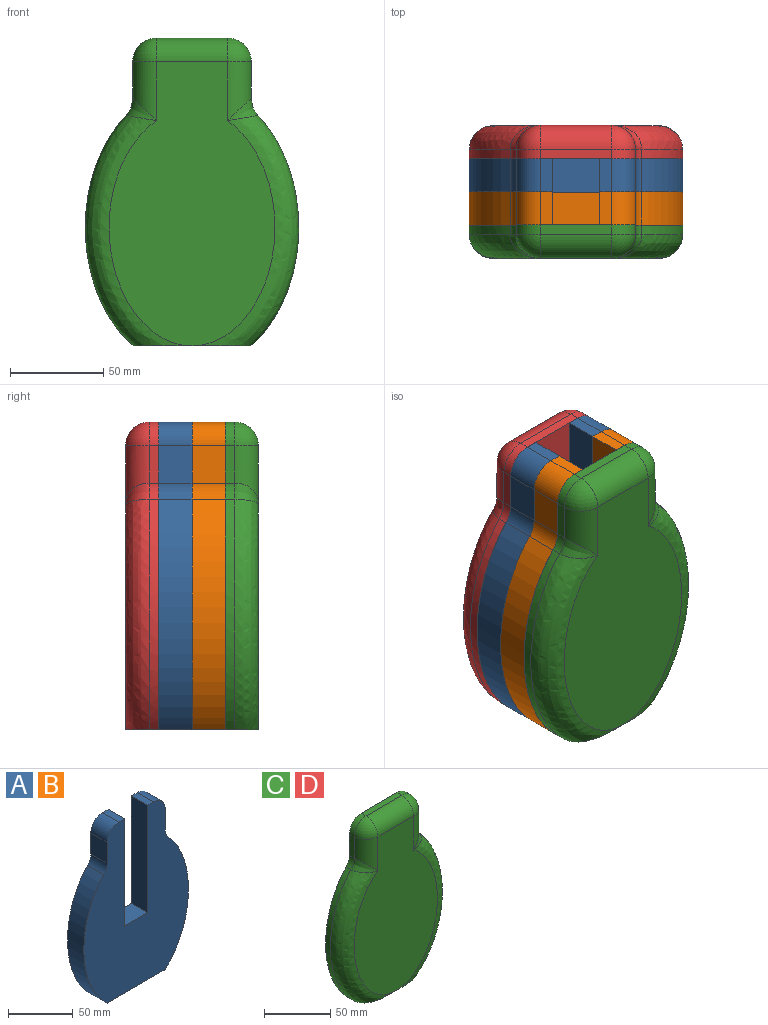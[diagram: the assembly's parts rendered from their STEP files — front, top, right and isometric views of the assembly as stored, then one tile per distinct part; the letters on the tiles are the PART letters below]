
ASSEMBLY  parts=4 mates=6
PART A: 16 faces, bbox 114.3x17.8x165 mm
  f0: plane 17.78x6.35mm, normal (0,0,1), area 112.9mm2, adj f7,f8,f12,f13
  f1: extruded ~123.46x25.55mm, area 2414.5mm2, adj f6,f7,f8,f10
  f2: plane 20.03x17.78mm, normal (1,0,0), area 356mm2, adj f7,f8,f10,f11
  f3: plane 17.78x6.35mm, normal (0,0,1), area 112.9mm2, adj f7,f8,f11,f15
  f4: plane 20.03x17.78mm, normal (-1,0,0), area 356mm2, adj f7,f8,f9,f12
  f5: extruded ~123.46x25.55mm, area 2414.5mm2, adj f6,f7,f8,f9
  f6: plane 63.18x17.78mm, normal (0,0,-1), area 1123.4mm2, adj f1,f5,f7,f8
  f7: plane 164.96x114.3mm, normal (0,-1,0), area 12359.6mm2, adj f0,f1,f2,f3,f4,f5,f6,f9
  f8: plane 164.96x114.3mm, normal (0,1,0), area 12359.6mm2, adj f0,f1,f2,f3,f4,f5,f6,f9
  f9: cylinder r=12.7mm len=17.78mm, axis (0,1,0), area 172.3mm2, adj f4,f5,f7,f8
  f10: cylinder r=12.7mm len=17.78mm, axis (0,1,0), area 172.3mm2, adj f1,f2,f7,f8
  f11: cylinder r=12.7mm len=17.78mm, axis (0,1,0), area 354.7mm2, adj f2,f3,f7,f8
  f12: cylinder r=12.7mm len=17.78mm, axis (0,-1,0), area 354.7mm2, adj f0,f4,f7,f8
  f13: plane 101.6x17.78mm, normal (1,0,0), area 1806.4mm2, adj f0,f7,f8,f14
  f14: plane 25.4x17.78mm, normal (0,0,1), area 451.6mm2, adj f7,f8,f13,f15
  f15: plane 101.6x17.78mm, normal (-1,0,0), area 1806.4mm2, adj f3,f7,f8,f14
PART B: same geometry as A
PART C: 21 faces, bbox 128.2x31.7x191.6 mm
  f0: extruded ~123.46x25.55mm, area 689.8mm2, adj f5,f7,f12,f19
  f1: plane 20.03x5.08mm, normal (1,0,0), area 101.7mm2, adj f7,f11,f17,f19
  f2: plane 38.1x5.08mm, normal (0,0,1), area 193.5mm2, adj f7,f10,f15,f17
  f3: plane 20.03x5.08mm, normal (-1,0,0), area 101.7mm2, adj f7,f9,f13,f15
  f4: extruded ~123.46x25.55mm, area 689.8mm2, adj f5,f7,f8,f13
  f5: plane 77.08x31.67mm, normal (0,0,-1), area 1008.3mm2, adj f0,f4,f7,f8,f12
  f6: plane 152.27x88.9mm, normal (0,-1,0), area 9881mm2, adj f8,f9,f10,f11,f12
  f7: plane 164.96x114.3mm, normal (0,1,0), area 14940.2mm2, adj f0,f1,f2,f3,f4,f5,f13,f15
  f8: bspline ~144.89x62.03mm, area 2958.3mm2, adj f4,f5,f6,f14
  f9: cylinder r=12.7mm len=31.53mm, axis (0,0,1), area 514.3mm2, adj f3,f6,f14,f16
  f10: cylinder r=12.7mm len=38.1mm, axis (1,0,0), area 760.1mm2, adj f2,f6,f16,f18
  f11: cylinder r=12.7mm len=31.53mm, axis (0,0,-1), area 514.3mm2, adj f1,f6,f18,f20
  f12: bspline ~145.77x59.48mm, area 2958.7mm2, adj f0,f5,f6,f20
  f13: cylinder r=12.7mm len=8.78mm, axis (0,1,0), area 49.2mm2, adj f3,f4,f7,f14
  f14: bspline ~16.23x13.61mm, area 82.5mm2, adj f8,f9,f13
  f15: cylinder r=12.7mm len=12.7mm, axis (0,-1,0), area 101.3mm2, adj f2,f3,f7,f16
  f16: sphere r=12.7mm, area 253.4mm2, adj f9,f10,f15
  f17: cylinder r=12.7mm len=12.7mm, axis (0,1,0), area 101.3mm2, adj f1,f2,f7,f18
  f18: sphere r=12.7mm, area 253.4mm2, adj f10,f11,f17
  f19: cylinder r=12.7mm len=8.78mm, axis (0,1,0), area 49.2mm2, adj f0,f1,f7,f20
  f20: bspline ~16.23x13.61mm, area 82.5mm2, adj f11,f12,f19
PART D: same geometry as C
PLACE A t=(0,35.56,0)mm
PLACE B t=(0,17.78,0)mm
PLACE C at identity fixed
PLACE D rot(axis=(0,0,1),180deg) t=(0,35.56,0)mm
MATE planar C.f5 <-> A.f6  axis (0,0,-1) through (0,-8.18,0)mm
MATE planar D.f5 <-> C.f5  axis (0,0,-1) through (0,43.74,0)mm
MATE planar C.f5 <-> B.f6  axis (0,0,-1) through (0,-8.18,0)mm
MATE planar C.f7 <-> B.f7  axis (0,1,0) through (0,0,76.38)mm
MATE planar D.f7 <-> A.f8  axis (0,-1,0) through (0,35.56,76.38)mm
MATE planar B.f8 <-> A.f7  axis (0,1,0) through (0,17.78,68.49)mm
